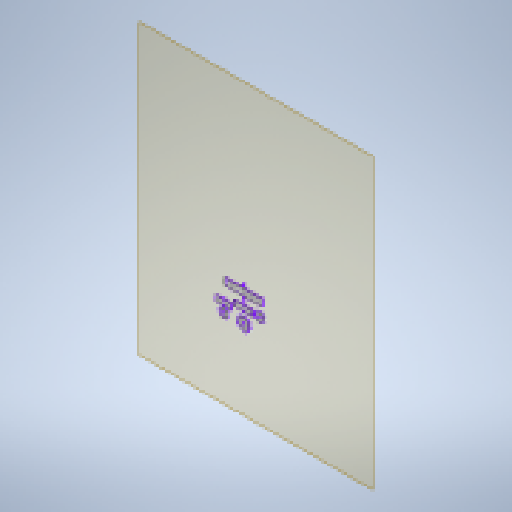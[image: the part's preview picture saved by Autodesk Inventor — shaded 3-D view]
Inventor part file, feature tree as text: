
AUTODESK INVENTOR PART (.ipt)
format: ipt  version: 2023 (Build 270158030, 158C)  size: 236,032 bytes
history: native  units: mm
features: other x10, sketch x4, plane x1, extrude x1
ambient origin geometry x8: Origin, YZ Plane, XZ Plane, XY Plane, X Axis, Y Axis, Z Axis, Center Point
bodies: Body1 (feature_tree)
feature tree (16):
  other  "mode-select-layout"
  plane  "Work Plane1"
  extrude  "Extrusion1"  Depth=22.0mm
  other  "Decal1"
  other  "Decal2"
  other  "Decal3"
  sketch  "Sketch1"  dims[d0=22.0mm d1=22.0mm]
  sketch  "Sketch5"  dims[d2=90.0mm]
  other  "Image3"
  sketch  "Sketch6"  dims[d7=29.0mm]
  other  "Image6"
  sketch  "Sketch7"  dims[d8=16.0mm d9=16.0mm d10=20.0mm d11=20.0mm d12=30.0mm d14=40.0mm d17=37.0mm d18=20.0mm d19=10.0mm d20=10.0mm d21=30.0mm d22=35.0mm d24=1.0mm d25=0.0mm d26=39.051248mm d28=4.3mm d29=4.8mm d30=10.0mm d31=10.0mm d124=10.813395mm d125=9.186605mm d126=12.0mm d130=1.6mm d131=1.6mm d132=2.0mm]
  other  "Image7"
  other  "<userpath>\Documents\0004-inventor\Inventor_Projects\electronics-enclosure\enclosure.iam"
  other  "enclosure.iam"
  other  "door:1"
